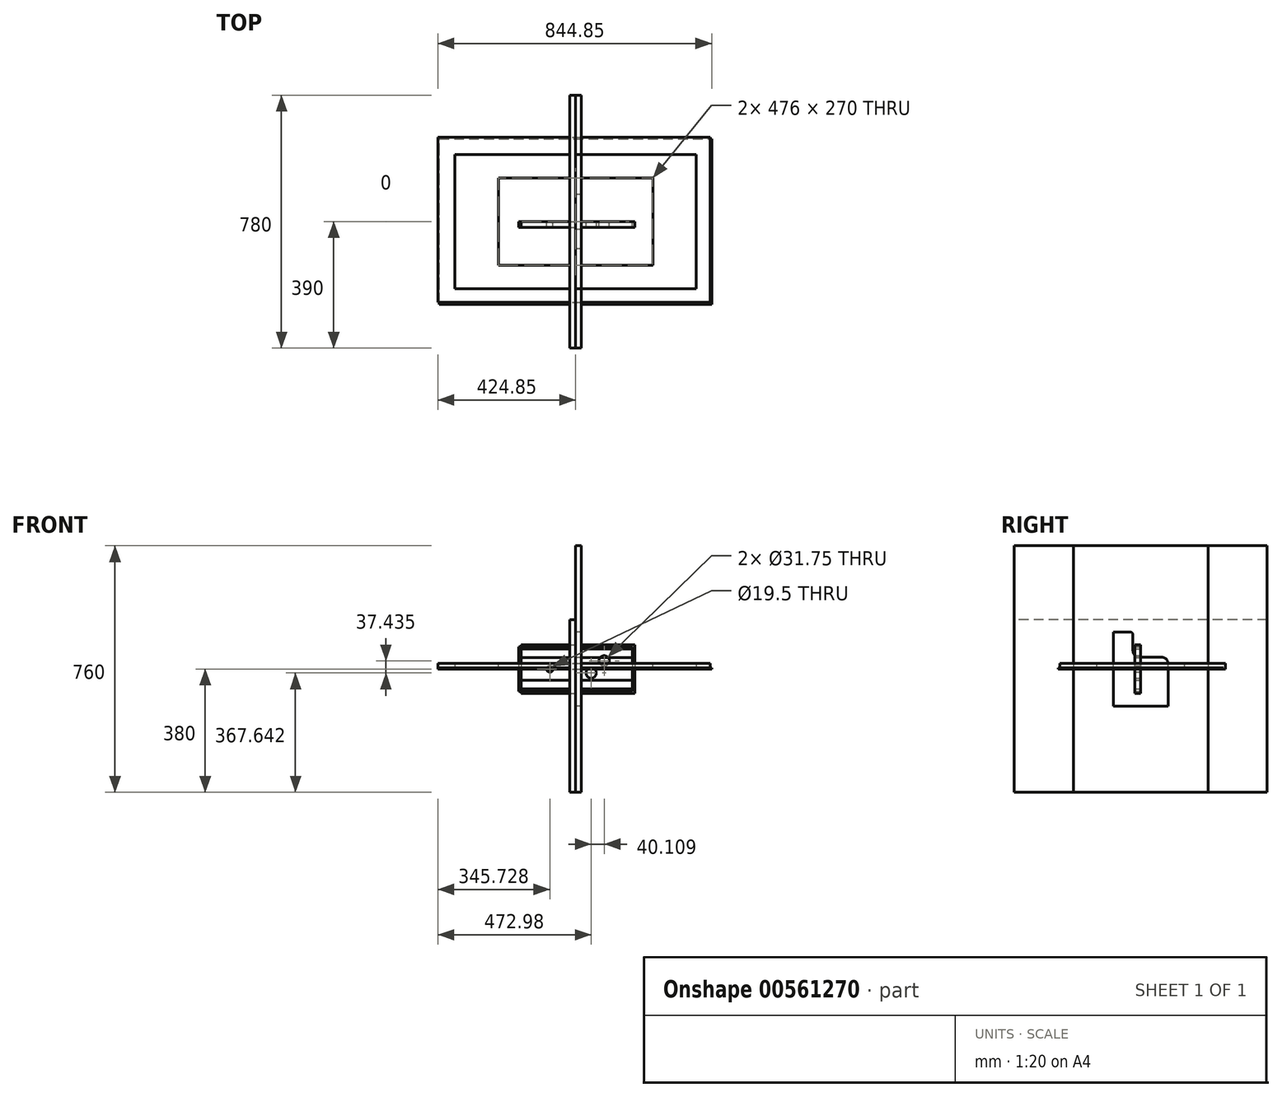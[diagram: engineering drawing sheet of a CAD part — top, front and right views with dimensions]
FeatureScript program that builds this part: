
annotation { "Feature Type Name" : "Feature", "Feature Type Description" : "" }
export const myFeature = defineFeature(function(context is Context, id is Id, definition is map)
    precondition{}
    {
        {
            var Q0;
            Q0=qCreatedBy(makeId("Top.planeOp"),FACE);
            var sketch = newSketch(context, id + "F0", { "sketchPlane" : qUnion([Q0])});
            skLineSegment(sketch, "E0.bottom", {"start": v(-424.85, 260.98) * mm, "end": v(415.15, 260.98) * mm});
            skLineSegment(sketch, "E0.top", {"start": v(-424.85, -249.02) * mm, "end": v(415.15, -249.02) * mm});
            skLineSegment(sketch, "E0.left", {"start": v(-424.85, 260.98) * mm, "end": v(-424.85, -249.02) * mm});
            skLineSegment(sketch, "E0.right", {"start": v(415.15, 260.98) * mm, "end": v(415.15, -249.02) * mm});
            skSolve(sketch);
        }
        {
            var Q0;
            Q0=makeQuery(id+"F0.imprint","IMPRINT",FACE,{"disambiguationData":[TD([[makeQuery(id+"F0.imprint","IMPRINT",EDGE,{"derivedFrom":sQuery(id+"F0.wireOp",EDGE,"E0.bottom")}),-1.0]])]});
            extrude(context, id + "F1", {"entities" : qUnion([Q0]), "depth" : 3 * mm, "offsetDistance" : 25 * mm});
        }
        {
            var Q0;
            Q0=makeQuery(id+"F0.imprint","IMPRINT",FACE,{"disambiguationData":[TD([[makeQuery(id+"F0.imprint","IMPRINT",EDGE,{"derivedFrom":sQuery(id+"F0.wireOp",EDGE,"E0.bottom")}),-1.0]])]});
            extrude(context, id + "F2", {"entities" : qUnion([Q0]), "operationType" : NewBodyOperationType.ADD, "depth" : 17.6 * mm, "offsetDistance" : 25 * mm});
        }
        {
            var Q0;
            Q0=makeQuery(id+"F2.opExtrude","CAP_FACE",FACE,{"disambiguationData":[OSD([sQuery(id+"F0.wireOp",EDGE,"E0.bottom"),sQuery(id+"F0.wireOp",EDGE,"E0.top"),sQuery(id+"F0.wireOp",EDGE,"E0.left"),sQuery(id+"F0.wireOp",EDGE,"E0.right")])],"isStart":false});
            var sketch = newSketch(context, id + "F3", { "sketchPlane" : qUnion([Q0])});
            skLineSegment(sketch, "E1.bottom", {"start": v(-238, -135) * mm, "end": v(238, -135) * mm});
            skLineSegment(sketch, "E1.top", {"start": v(-238, 135) * mm, "end": v(238, 135) * mm});
            skLineSegment(sketch, "E1.left", {"start": v(-238, -135) * mm, "end": v(-238, 135) * mm});
            skLineSegment(sketch, "E1.right", {"start": v(238, -135) * mm, "end": v(238, 135) * mm});
            skPoint(sketch, "E1.middle", {"position": v(0, 0) * mm});
            skSolve(sketch);
        }
        {
            var Q0;
            Q0=qCreatedBy(makeId("Top.planeOp"),FACE);
            var sketch = newSketch(context, id + "F4", { "sketchPlane" : qUnion([Q0])});
            skLineSegment(sketch, "E2.bottom", {"start": v(-420, -255) * mm, "end": v(420, -255) * mm});
            skLineSegment(sketch, "E2.top", {"start": v(-420, 255) * mm, "end": v(420, 255) * mm});
            skLineSegment(sketch, "E2.left", {"start": v(-420, -255) * mm, "end": v(-420, 255) * mm});
            skLineSegment(sketch, "E2.right", {"start": v(420, -255) * mm, "end": v(420, 255) * mm});
            skPoint(sketch, "E2.middle", {"position": v(0, 0) * mm});
            skSolve(sketch);
        }
        {
            var Q0;
            Q0=makeQuery(id+"F4.imprint","IMPRINT",FACE,{"disambiguationData":[TD([[makeQuery(id+"F4.imprint","IMPRINT",EDGE,{"derivedFrom":sQuery(id+"F4.wireOp",EDGE,"E2.bottom")}),1.0]])]});
            extrude(context, id + "F5", {"entities" : qUnion([Q0]), "depth" : 3 * mm, "offsetDistance" : 25 * mm});
        }
        {
            var Q0;
            Q0=makeQuery(id+"F3.imprint","IMPRINT",FACE,{"disambiguationData":[TD([[makeQuery(id+"F3.imprint","IMPRINT",EDGE,{"derivedFrom":sQuery(id+"F3.wireOp",EDGE,"E1.bottom")}),1.0]])]});
            extrude(context, id + "F6", {"entities" : qUnion([Q0]), "operationType" : NewBodyOperationType.REMOVE, "oppositeDirection" : true, "depth" : 25 * mm, "offsetDistance" : 25 * mm});
        }
        {
            var Q0;
            Q0=qCreatedBy(makeId("Right.planeOp"),FACE);
            var sketch = newSketch(context, id + "F7", { "sketchPlane" : qUnion([Q0])});
            skLineSegment(sketch, "E3.bottom", {"start": v(390, 380) * mm, "end": v(-390, 380) * mm});
            skLineSegment(sketch, "E3.top", {"start": v(390, -380) * mm, "end": v(-390, -380) * mm});
            skLineSegment(sketch, "E3.left", {"start": v(390, 380) * mm, "end": v(390, -380) * mm});
            skLineSegment(sketch, "E3.right", {"start": v(-390, 380) * mm, "end": v(-390, -380) * mm});
            skPoint(sketch, "E3.middle", {"position": v(0, 0) * mm});
            skLineSegment(sketch, "E4.bottom", {"start": v(390, 380) * mm, "end": v(192.5, 380) * mm});
            skLineSegment(sketch, "E4.top", {"start": v(390, 152) * mm, "end": v(192.5, 152) * mm});
            skLineSegment(sketch, "E4.left", {"start": v(390, 380) * mm, "end": v(390, 152) * mm});
            skLineSegment(sketch, "E4.right", {"start": v(192.5, 380) * mm, "end": v(192.5, 152) * mm});
            skLineSegment(sketch, "E5.bottom", {"start": v(-390, 380) * mm, "end": v(-192.5, 380) * mm});
            skLineSegment(sketch, "E5.top", {"start": v(-390, 152) * mm, "end": v(-192.5, 152) * mm});
            skLineSegment(sketch, "E5.left", {"start": v(-390, 380) * mm, "end": v(-390, 152) * mm});
            skLineSegment(sketch, "E5.right", {"start": v(-192.5, 380) * mm, "end": v(-192.5, 152) * mm});
            skLineSegment(sketch, "E6", {"start": v(192.5, 152) * mm, "end": v(-192.5, 152) * mm});
            skSolve(sketch);
        }
        {
            var Q0;
            Q0=makeQuery(id+"F7.imprint","IMPRINT",FACE,{"disambiguationData":[TD([[makeQuery(id+"F7.imprint","IMPRINT",EDGE,{"derivedFrom":sQuery(id+"F7.wireOp",EDGE,"E3.top")}),-1.0]])]});
            var Q1;
            Q1=makeQuery(id+"F7.imprint","IMPRINT",FACE,{"disambiguationData":[TD([[makeQuery(id+"F7.imprint","IMPRINT",EDGE,{"derivedFrom":sQuery(id+"F7.wireOp",EDGE,"E4.bottom")}),1.0]])]});
            var Q2;
            Q2=makeQuery(id+"F7.imprint","IMPRINT",FACE,{"disambiguationData":[TD([[makeQuery(id+"F7.imprint","IMPRINT",EDGE,{"derivedFrom":sQuery(id+"F7.wireOp",EDGE,"E5.bottom")}),-1.0]])]});
            extrude(context, id + "F8", {"entities" : qUnion([Q0, Q1, Q2]), "oppositeDirection" : true, "depth" : 17.6 * mm, "offsetDistance" : 25 * mm});
        }
        {
            var Q0;
            Q0=qCreatedBy(makeId("Right.planeOp"),FACE);
            var sketch = newSketch(context, id + "F9", { "sketchPlane" : qUnion([Q0])});
            skLineSegment(sketch, "E7.bottom", {"start": v(84, -114.5) * mm, "end": v(-84, -114.5) * mm});
            skLineSegment(sketch, "E7.top", {"start": v(84, 114.5) * mm, "end": v(-84, 114.5) * mm});
            skLineSegment(sketch, "E7.left", {"start": v(84, -114.5) * mm, "end": v(84, 114.5) * mm});
            skLineSegment(sketch, "E7.right", {"start": v(-84, -114.5) * mm, "end": v(-84, 114.5) * mm});
            skPoint(sketch, "E7.middle", {"position": v(0, 0) * mm});
            skLineSegment(sketch, "E8.bottom", {"start": v(-84, 114.5) * mm, "end": v(-34, 114.5) * mm});
            skLineSegment(sketch, "E8.left", {"start": v(-84, 114.5) * mm, "end": v(-84, 36.5) * mm});
            skLineSegment(sketch, "E8.right", {"start": v(-24, 104.5) * mm, "end": v(-24, 56.5) * mm});
            skPoint(sketch, "E9.visualSharp", {"position": v(-24, 114.5) * mm});
            skArc(sketch, "E9.filletArc", {"start": v(-24, 104.5) * mm, "mid": v(-26.93, 111.57) * mm, "end": v(-34, 114.5) * mm});
            skPoint(sketch, "E10.visualSharp", {"position": v(-24, 36.5) * mm});
            skArc(sketch, "E10.filletArc", {"start": v(-24, 56.5) * mm, "mid": v(-18.14, 42.36) * mm, "end": v(-4, 36.5) * mm});
            skLineSegment(sketch, "E11", {"start": v(-4, 36.5) * mm, "end": v(84, 36.5) * mm});
            skSolve(sketch);
        }
        {
            var Q0;
            {var subQ1=sQuery(id+"F9.wireOp",EDGE,"E7.bottom");Q0=makeQuery(id+"F9.imprint","IMPRINT",FACE,{"disambiguationData":[TD([[makeQuery(id+"F9.imprint","IMPRINT",EDGE,{"derivedFrom":subQ1}),-1.0]])]});}
            extrude(context, id + "F10", {"entities" : qUnion([Q0]), "depth" : 17.6 * mm, "offsetDistance" : 25 * mm});
        }
        {
            var Q0;
            Q0=makeQuery(id+"F10.opExtrude","CAP_FACE",FACE,{"disambiguationData":[OSD([sQuery(id+"F9.wireOp",EDGE,"E7.bottom"),sQuery(id+"F9.wireOp",EDGE,"E7.left"),sQuery(id+"F9.wireOp",EDGE,"E7.right"),sQuery(id+"F9.wireOp",EDGE,"E8.bottom"),sQuery(id+"F9.wireOp",EDGE,"E8.left"),sQuery(id+"F9.wireOp",EDGE,"E8.right"),sQuery(id+"F9.wireOp",EDGE,"E9.filletArc"),sQuery(id+"F9.wireOp",EDGE,"E10.filletArc"),sQuery(id+"F9.wireOp",EDGE,"E11")])],"isStart":false});
            var sketch = newSketch(context, id + "F11", { "sketchPlane" : qUnion([Q0])});
            skLineSegment(sketch, "E12.bottom", {"start": v(64, 36.5) * mm, "end": v(0, 36.5) * mm});
            skLineSegment(sketch, "E12.top", {"start": v(84, 0) * mm, "end": v(0, 0) * mm});
            skLineSegment(sketch, "E12.left", {"start": v(84, 16.5) * mm, "end": v(84, 0) * mm});
            skLineSegment(sketch, "E12.right", {"start": v(0, 36.5) * mm, "end": v(0, 0) * mm});
            skPoint(sketch, "E13.visualSharp", {"position": v(84, 36.5) * mm});
            skArc(sketch, "E13.filletArc", {"start": v(84, 16.5) * mm, "mid": v(78.14, 30.64) * mm, "end": v(64, 36.5) * mm});
            skSolve(sketch);
        }
        {
            var Q0;
            {var subQ0=sQuery(id+"F11.wireOp",EDGE,"E13.filletArc");Q0=makeQuery(id+"F11.imprint","IMPRINT",FACE,{"disambiguationData":[TD([[makeQuery(id+"F11.imprint","IMPRINT",EDGE,{"derivedFrom":subQ0}),-1.0]])]});}
            extrude(context, id + "F12", {"entities" : qUnion([Q0]), "operationType" : NewBodyOperationType.REMOVE, "oppositeDirection" : true, "depth" : 17.6 * mm, "offsetDistance" : 25 * mm});
        }
        {
            var Q0;
            Q0=qCreatedBy(makeId("Right.planeOp"),FACE);
            var sketch = newSketch(context, id + "F13", { "sketchPlane" : qUnion([Q0])});
            skLineSegment(sketch, "E14.bottom", {"start": v(-207.5, -380) * mm, "end": v(207.5, -380) * mm});
            skLineSegment(sketch, "E14.top", {"start": v(-207.5, 380) * mm, "end": v(207.5, 380) * mm});
            skLineSegment(sketch, "E14.left", {"start": v(-207.5, -380) * mm, "end": v(-207.5, 380) * mm});
            skLineSegment(sketch, "E14.right", {"start": v(207.5, -380) * mm, "end": v(207.5, 380) * mm});
            skPoint(sketch, "E14.middle", {"position": v(0, 0) * mm});
            skSolve(sketch);
        }
        {
            var Q0;
            Q0 = qSketchRegion(id + "F13", true);
            extrude(context, id + "F14", {"entities" : qUnion([Q0]), "depth" : 17.6 * mm, "offsetDistance" : 25 * mm});
        }
        {
            var Q0;
            Q0 = qSketchRegion(id + "F7", true);
            extrude(context, id + "F15", {"entities" : qUnion([Q0]), "depth" : 17.6 * mm, "offsetDistance" : 25 * mm});
        }
        {
            var Q0;
            Q0=qCreatedBy(makeId("Top.planeOp"),FACE);
            var sketch = newSketch(context, id + "F16", { "sketchPlane" : qUnion([Q0])});
            skLineSegment(sketch, "E15.bottom", {"start": v(-372.5, -207.5) * mm, "end": v(372.5, -207.5) * mm});
            skLineSegment(sketch, "E15.top", {"start": v(-372.5, 207.5) * mm, "end": v(372.5, 207.5) * mm});
            skLineSegment(sketch, "E15.left", {"start": v(-372.5, -207.5) * mm, "end": v(-372.5, 207.5) * mm});
            skLineSegment(sketch, "E15.right", {"start": v(372.5, -207.5) * mm, "end": v(372.5, 207.5) * mm});
            skPoint(sketch, "E15.middle", {"position": v(0, 0) * mm});
            skSolve(sketch);
        }
        {
            var Q0;
            Q0 = qSketchRegion(id + "F16", true);
            extrude(context, id + "F17", {"entities" : qUnion([Q0]), "depth" : 17.6 * mm, "offsetDistance" : 25 * mm});
        }
        {
            var Q0;
            Q0=qCreatedBy(makeId("Front.planeOp"),FACE);
            var sketch = newSketch(context, id + "F18", { "sketchPlane" : qUnion([Q0])});
            skLineSegment(sketch, "E16.bottom", {"start": v(-175, 61.5) * mm, "end": v(175, 61.5) * mm});
            skLineSegment(sketch, "E16.top", {"start": v(-175, -61.5) * mm, "end": v(175, -61.5) * mm});
            skLineSegment(sketch, "E16.left", {"start": v(-175, 61.5) * mm, "end": v(-175, -61.5) * mm});
            skLineSegment(sketch, "E16.right", {"start": v(175, 61.5) * mm, "end": v(175, -61.5) * mm});
            skPoint(sketch, "E16.middle", {"position": v(0, 0) * mm});
            skSolve(sketch);
        }
        {
            var Q0;
            Q0 = qSketchRegion(id + "F18", true);
            extrude(context, id + "F19", {"entities" : qUnion([Q0]), "depth" : 17.6 * mm, "offsetDistance" : 25 * mm});
        }
        {
            var Q0;
            Q0=qCreatedBy(makeId("Front.planeOp"),FACE);
            var sketch = newSketch(context, id + "F20", { "sketchPlane" : qUnion([Q0])});
            skLineSegment(sketch, "E17.bottom", {"start": v(-167.88, 75) * mm, "end": v(182.12, 75) * mm});
            skLineSegment(sketch, "E17.top", {"start": v(-167.88, -75) * mm, "end": v(182.12, -75) * mm});
            skLineSegment(sketch, "E17.left", {"start": v(-167.88, 75) * mm, "end": v(-167.88, -75) * mm});
            skLineSegment(sketch, "E17.right", {"start": v(182.12, 75) * mm, "end": v(182.12, -75) * mm});
            skPoint(sketch, "E17.middle", {"position": v(7.12, 0) * mm});
            skCircle(sketch, "E18", {"center": v(-79.12, 0) * mm, "radius": 9.75 * mm});
            skCircle(sketch, "E19", {"center": v(48.13, -12.36) * mm, "radius": 15.88 * mm});
            skCircle(sketch, "E20", {"center": v(88.24, 25.08) * mm, "radius": 15.88 * mm});
            skSolve(sketch);
        }
        {
            var Q0;
            Q0=makeQuery(id+"F20.imprint","IMPRINT",FACE,{"disambiguationData":[TD([[makeQuery(id+"F20.imprint","IMPRINT",EDGE,{"derivedFrom":sQuery(id+"F20.wireOp",EDGE,"E17.bottom")}),-1.0]])]});
            extrude(context, id + "F21", {"entities" : qUnion([Q0]), "depth" : 17.6 * mm, "offsetDistance" : 25 * mm});
        }
        {
            var Q0;
            Q0=qCreatedBy(makeId("Front.planeOp"),FACE);
            var sketch = newSketch(context, id + "F22", { "sketchPlane" : qUnion([Q0])});
            skLineSegment(sketch, "E21.bottom", {"start": v(-175, -35) * mm, "end": v(175, -35) * mm});
            skLineSegment(sketch, "E21.top", {"start": v(-175, 35) * mm, "end": v(175, 35) * mm});
            skLineSegment(sketch, "E21.left", {"start": v(-175, -35) * mm, "end": v(-175, 35) * mm});
            skLineSegment(sketch, "E21.right", {"start": v(175, -35) * mm, "end": v(175, 35) * mm});
            skPoint(sketch, "E21.middle", {"position": v(0, 0) * mm});
            skSolve(sketch);
        }
        {
            var Q0;
            Q0 = qSketchRegion(id + "F22", true);
            extrude(context, id + "F23", {"entities" : qUnion([Q0]), "depth" : 17.6 * mm, "offsetDistance" : 25 * mm});
        }
        {
            var Q0;
            Q0=qCreatedBy(makeId("Front.planeOp"),FACE);
            var sketch = newSketch(context, id + "F24", { "sketchPlane" : qUnion([Q0])});
            skLineSegment(sketch, "E22.bottom", {"start": v(-175, -68.5) * mm, "end": v(175, -68.5) * mm});
            skLineSegment(sketch, "E22.top", {"start": v(-175, 68.5) * mm, "end": v(175, 68.5) * mm});
            skLineSegment(sketch, "E22.left", {"start": v(-175, -68.5) * mm, "end": v(-175, 68.5) * mm});
            skLineSegment(sketch, "E22.right", {"start": v(175, -68.5) * mm, "end": v(175, 68.5) * mm});
            skPoint(sketch, "E22.middle", {"position": v(0, 0) * mm});
            skSolve(sketch);
        }
        {
            var Q0;
            Q0 = qSketchRegion(id + "F24", true);
            extrude(context, id + "F25", {"entities" : qUnion([Q0]), "depth" : 17.6 * mm, "offsetDistance" : 25 * mm});
        }
        {
            var Q0;
            Q0=qCreatedBy(makeId("Top.planeOp"),FACE);
            var sketch = newSketch(context, id + "F26", { "sketchPlane" : qUnion([Q0])});
            skLineSegment(sketch, "E23.bottom", {"start": v(-372.4, -207.5) * mm, "end": v(372.4, -207.5) * mm});
            skLineSegment(sketch, "E23.top", {"start": v(-372.4, 207.5) * mm, "end": v(372.4, 207.5) * mm});
            skLineSegment(sketch, "E23.left", {"start": v(-372.4, -207.5) * mm, "end": v(-372.4, 207.5) * mm});
            skLineSegment(sketch, "E23.right", {"start": v(372.4, -207.5) * mm, "end": v(372.4, 207.5) * mm});
            skPoint(sketch, "E23.middle", {"position": v(0, 0) * mm});
            skSolve(sketch);
        }
        {
            var Q0;
            Q0=makeQuery(id+"F26.imprint","IMPRINT",FACE,{"disambiguationData":[TD([[makeQuery(id+"F26.imprint","IMPRINT",EDGE,{"derivedFrom":sQuery(id+"F26.wireOp",EDGE,"E23.bottom")}),1.0]])]});
            extrude(context, id + "F27", {"entities" : qUnion([Q0]), "depth" : 17.6 * mm, "offsetDistance" : 25 * mm});
        }
    });
